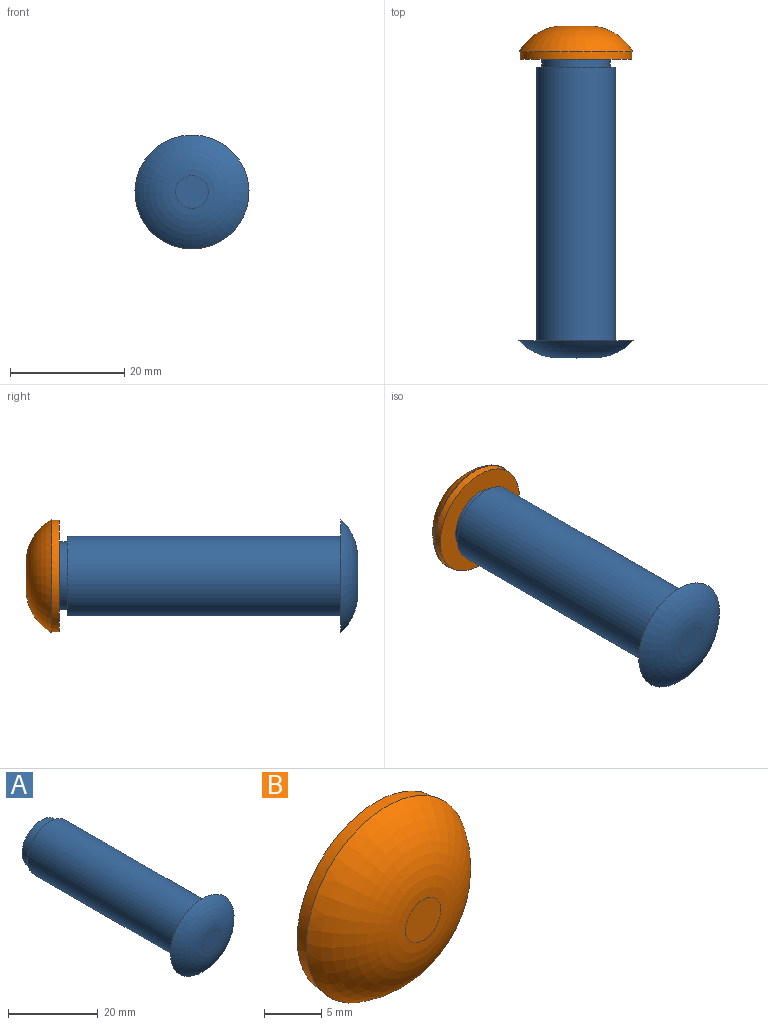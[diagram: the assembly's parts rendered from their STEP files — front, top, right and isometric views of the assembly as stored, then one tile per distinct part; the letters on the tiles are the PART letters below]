
ASSEMBLY  parts=2 mates=1
PART A: 7 faces, bbox 20x53.7x20 mm
  f0: cylinder r=7mm len=48mm, axis (0,1,0), area 2111.2mm2, adj f1,f3
  f1: plane 14x14mm, normal (0,1,0), area 40.8mm2, adj f0,f5
  f2: plane 5.72x5.72mm, normal (0,-1,0), area 25.7mm2, adj f4
  f3: plane 20x20mm, normal (0,1,0), area 160.2mm2, adj f0,f4
  f4: torus R=2.86mm, axis (0,1,0), area 331.4mm2, adj f2,f3
  f5: cylinder r=6mm len=12mm, axis (0,-1,0), area 101.8mm2, adj f1,f6
  f6: plane 12x12mm, normal (0,1,0), area 113.1mm2, adj f5
PART B: 7 faces, bbox 20x5.8x20 mm
  f0: plane 4.36x4.36mm, normal (0,-1,0), area 14.9mm2, adj f2
  f1: plane 19.95x19.95mm, normal (0,1,0), area 10.9mm2, adj f2,f3
  f2: torus R=2.18mm, axis (0,1,0), area 383.6mm2, adj f0,f1
  f3: cylinder r=9.8mm len=19.6mm, axis (0,-1,0), area 80mm2, adj f1,f4
  f4: plane 19.6x19.6mm, normal (0,1,0), area 188.6mm2, adj f3,f5
  f5: cylinder r=6mm len=12mm, axis (0,1,0), area 131.9mm2, adj f4,f6
  f6: plane 12x12mm, normal (0,1,0), area 113.1mm2, adj f5
PLACE A t=(4.74,46.44,37.3)mm
PLACE B rot(axis=(0,0,1),180deg) t=(6.39,49.14,37.3)mm
MATE planar B.f2 <-> A.f5  axis (0,-1,0) through (4.74,49.14,37.3)mm
